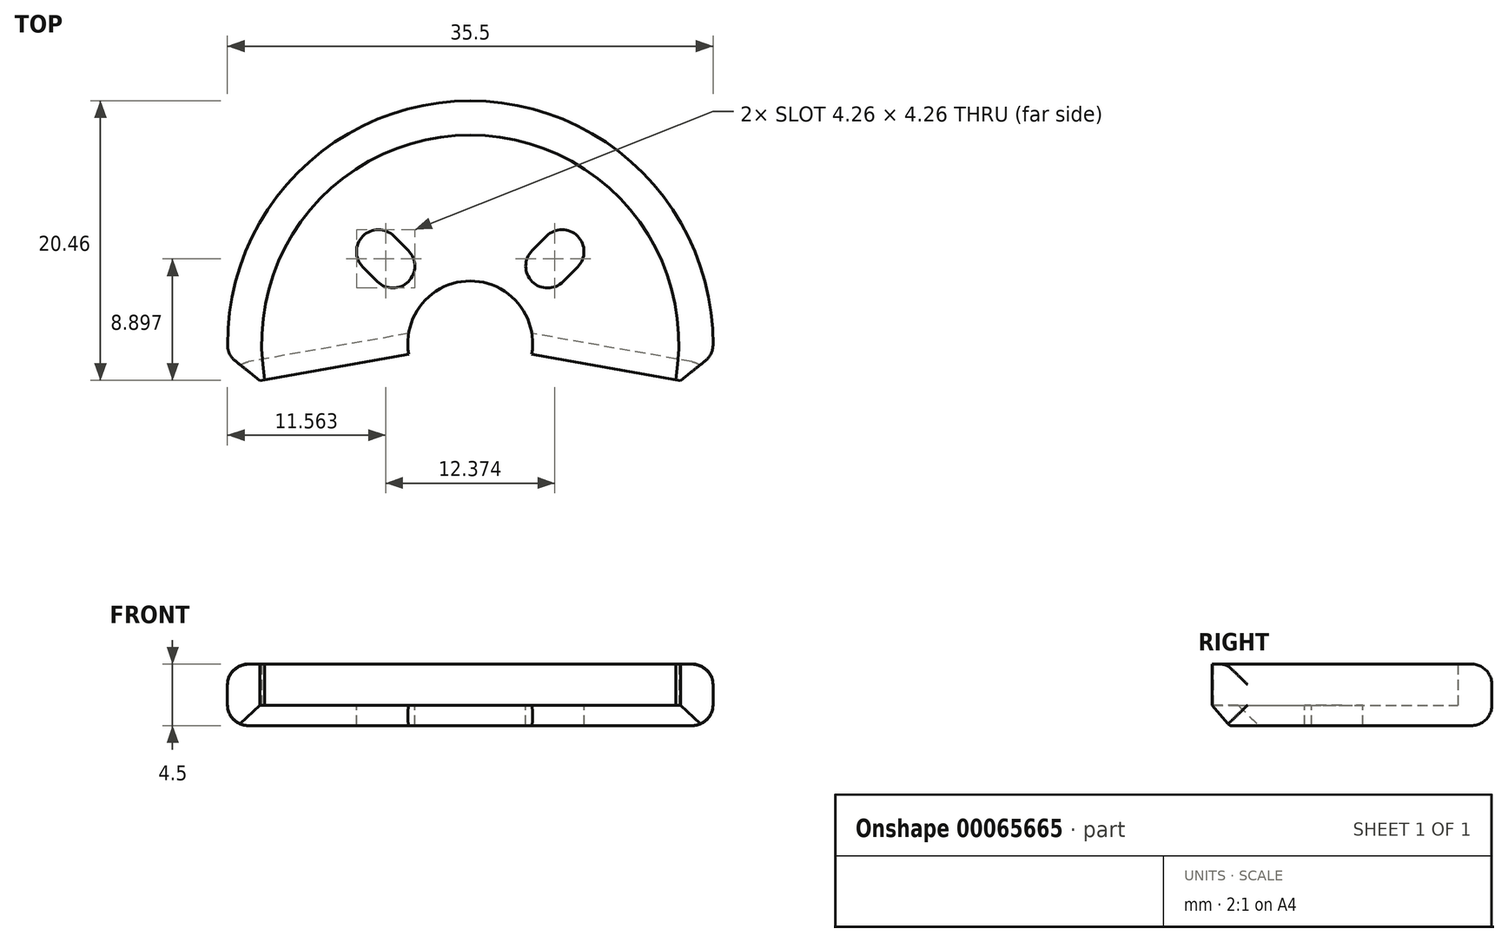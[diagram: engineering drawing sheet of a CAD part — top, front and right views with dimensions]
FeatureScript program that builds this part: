
annotation { "Feature Type Name" : "Feature", "Feature Type Description" : "" }
export const myFeature = defineFeature(function(context is Context, id is Id, definition is map)
    precondition{}
    {
        {
            var Q0;
            Q0=qCreatedBy(makeId("Top.planeOp"),FACE);
            var sketch = newSketch(context, id + "F0", { "sketchPlane" : qUnion([Q0])});
            skLineSegment(sketch, "E0", {"start": v(-4.5, -0.8) * mm, "end": v(-15.02, -2.65) * mm});
            skLineSegment(sketch, "E1", {"start": v(-15.02, -2.65) * mm, "end": v(-17.48, -3.08) * mm});
            skLineSegment(sketch, "E2", {"start": v(0, 0) * mm, "end": v(-5.66, 5.66) * mm, "construction": true});
            skLineSegment(sketch, "E3", {"start": v(-5.66, 5.66) * mm, "end": v(-6.72, 6.72) * mm, "construction": true});
            skArc(sketch, "E4.0.startCap", {"start": v(-4.53, 6.79) * mm, "mid": v(-4.53, 4.53) * mm, "end": v(-6.79, 4.53) * mm});
            skArc(sketch, "E4.0.endCap", {"start": v(-7.85, 5.59) * mm, "mid": v(-7.85, 7.85) * mm, "end": v(-5.59, 7.85) * mm});
            skLineSegment(sketch, "E4.0.left", {"start": v(-6.79, 4.53) * mm, "end": v(-7.85, 5.59) * mm});
            skLineSegment(sketch, "E4.0.right", {"start": v(-4.53, 6.79) * mm, "end": v(-5.59, 7.85) * mm});
            skLineSegment(sketch, "E5", {"start": v(0, 0) * mm, "end": v(-4.5, -0.8) * mm, "construction": true});
            skLineSegment(sketch, "E6.MirrorCS", {"start": v(4.5, -0.8) * mm, "end": v(15.02, -2.65) * mm});
            skLineSegment(sketch, "E7.MirrorCS", {"start": v(15.02, -2.65) * mm, "end": v(17.48, -3.08) * mm});
            skArc(sketch, "E8.MirrorCS", {"start": v(4.53, 6.79) * mm, "mid": v(4.53, 4.53) * mm, "end": v(6.79, 4.53) * mm});
            skArc(sketch, "E9.MirrorCS", {"start": v(7.85, 5.59) * mm, "mid": v(7.85, 7.85) * mm, "end": v(5.59, 7.85) * mm});
            skLineSegment(sketch, "E10.MirrorCS", {"start": v(4.53, 6.79) * mm, "end": v(5.59, 7.85) * mm});
            skLineSegment(sketch, "E11.MirrorCS", {"start": v(6.79, 4.53) * mm, "end": v(7.85, 5.59) * mm});
            skArc(sketch, "E12", {"start": v(-17.48, -3.08) * mm, "mid": v(0, 17.75) * mm, "end": v(17.48, -3.08) * mm});
            skArc(sketch, "E13", {"start": v(-15.02, -2.65) * mm, "mid": v(0, 15.25) * mm, "end": v(15.02, -2.65) * mm});
            skArc(sketch, "E14", {"start": v(-4.5, -0.8) * mm, "mid": v(0, 4.57) * mm, "end": v(4.5, -0.8) * mm});
            skSolve(sketch);
        }
        {
            var Q0;
            Q0=makeQuery(id+"F0.imprint","IMPRINT",FACE,{"disambiguationData":[TD([[makeQuery(id+"F0.imprint","IMPRINT",EDGE,{"derivedFrom":sQuery(id+"F0.wireOp",EDGE,"E1")}),-1.0]])]});
            extrude(context, id + "F1", {"entities" : qUnion([Q0]), "depth" : 3 * mm});
        }
        {
            var Q0;
            Q0=makeQuery(id+"F0.imprint","IMPRINT",FACE,{"disambiguationData":[TD([[makeQuery(id+"F0.imprint","IMPRINT",EDGE,{"derivedFrom":sQuery(id+"F0.wireOp",EDGE,"E1")}),-1.0]])]});
            var Q1;
            Q1=makeQuery(id+"F0.imprint","IMPRINT",FACE,{"disambiguationData":[TD([[makeQuery(id+"F0.imprint","IMPRINT",EDGE,{"derivedFrom":sQuery(id+"F0.wireOp",EDGE,"E0")}),-1.0]])]});
            extrude(context, id + "F2", {"entities" : qUnion([Q0, Q1]), "operationType" : NewBodyOperationType.ADD, "oppositeDirection" : true, "depth" : 1.5 * mm});
        }
        {
            var Q0;
            {var subQ0=sQuery(id+"F0.wireOp",EDGE,"E12");var subQ1=sQuery(id+"F0.wireOp",EDGE,"E1");Q0=makeQuery(id+"F2.boolean.opBoolean","MERGE",EDGE,{"derivedFrom":[makeQuery(id+"F1.opExtrude","SWEPT_EDGE",EDGE,{"disambiguationData":[OSD([subQ1,subQ0])]}),makeQuery(id+"F2.opExtrude","SWEPT_EDGE",EDGE,{"disambiguationData":[OSD([subQ1,subQ0])]})]});}
            var Q1;
            {var subQ0=sQuery(id+"F0.wireOp",EDGE,"E12");var subQ1=sQuery(id+"F0.wireOp",EDGE,"E7.MirrorCS");Q1=makeQuery(id+"F2.boolean.opBoolean","MERGE",EDGE,{"derivedFrom":[makeQuery(id+"F1.opExtrude","SWEPT_EDGE",EDGE,{"disambiguationData":[OSD([subQ1,subQ0])]}),makeQuery(id+"F2.opExtrude","SWEPT_EDGE",EDGE,{"disambiguationData":[OSD([subQ1,subQ0])]})]});}
            chamfer(context, id + "F3", {"entities" : qUnion([Q0, Q1]), "width" : 2 * mm, "tangentPropagation" : true});
        }
        {
            var Q0;
            Q0=makeQuery(id+"F2.opExtrude","CAP_EDGE",EDGE,{"disambiguationData":[OSD([sQuery(id+"F0.wireOp",EDGE,"E6.MirrorCS"),sQuery(id+"F0.wireOp",EDGE,"E7.MirrorCS")])],"isStart":false});
            var Q1;
            Q1=makeQuery(id+"F2.opExtrude","CAP_EDGE",EDGE,{"disambiguationData":[OSD([sQuery(id+"F0.wireOp",EDGE,"E0"),sQuery(id+"F0.wireOp",EDGE,"E1")])],"isStart":false});
            chamfer(context, id + "F4", {"entities" : qUnion([Q0, Q1]), "width" : 1.5 * mm, "tangentPropagation" : true});
        }
        {
            var Q0;
            Q0=makeQuery(id+"F1.opExtrude","CAP_EDGE",EDGE,{"disambiguationData":[OSD([sQuery(id+"F0.wireOp",EDGE,"E12")])],"isStart":false});
            var Q1;
            Q1=makeQuery(id+"F2.opExtrude","CAP_EDGE",EDGE,{"disambiguationData":[OSD([sQuery(id+"F0.wireOp",EDGE,"E12")])],"isStart":false});
            var Q2;
            {var subQ0=sQuery(id+"F0.wireOp",EDGE,"E12");var subQ1=sQuery(id+"F0.wireOp",EDGE,"E1");Q2=makeQuery(id+"F3.opChamfer","BLEND_EDGE",EDGE,{"blendedFrom":[makeQuery(id+"F2.boolean.opBoolean","MERGE",EDGE,{"derivedFrom":[makeQuery(id+"F1.opExtrude","SWEPT_EDGE",EDGE,{"disambiguationData":[OSD([subQ1,subQ0])]}),makeQuery(id+"F2.opExtrude","SWEPT_EDGE",EDGE,{"disambiguationData":[OSD([subQ1,subQ0])]})]}),makeQuery(id+"F2.boolean.opBoolean","MERGE",FACE,{"derivedFrom":[makeQuery(id+"F1.opExtrude","SWEPT_FACE",FACE,{"disambiguationData":[OSD([subQ0])]}),makeQuery(id+"F2.opExtrude","SWEPT_FACE",FACE,{"disambiguationData":[OSD([subQ0])]})]})],"blendedInto":[makeQuery(id+"F2.boolean.opBoolean","MERGE",FACE,{"derivedFrom":[makeQuery(id+"F1.opExtrude","SWEPT_FACE",FACE,{"disambiguationData":[OSD([subQ0])]}),makeQuery(id+"F2.opExtrude","SWEPT_FACE",FACE,{"disambiguationData":[OSD([subQ0])]})]})]});}
            var Q3;
            {var subQ0=sQuery(id+"F0.wireOp",EDGE,"E12");var subQ1=sQuery(id+"F0.wireOp",EDGE,"E7.MirrorCS");Q3=makeQuery(id+"F3.opChamfer","BLEND_EDGE",EDGE,{"blendedFrom":[makeQuery(id+"F2.boolean.opBoolean","MERGE",EDGE,{"derivedFrom":[makeQuery(id+"F1.opExtrude","SWEPT_EDGE",EDGE,{"disambiguationData":[OSD([subQ1,subQ0])]}),makeQuery(id+"F2.opExtrude","SWEPT_EDGE",EDGE,{"disambiguationData":[OSD([subQ1,subQ0])]})]}),makeQuery(id+"F2.boolean.opBoolean","MERGE",FACE,{"derivedFrom":[makeQuery(id+"F1.opExtrude","SWEPT_FACE",FACE,{"disambiguationData":[OSD([subQ0])]}),makeQuery(id+"F2.opExtrude","SWEPT_FACE",FACE,{"disambiguationData":[OSD([subQ0])]})]})],"blendedInto":[makeQuery(id+"F2.boolean.opBoolean","MERGE",FACE,{"derivedFrom":[makeQuery(id+"F1.opExtrude","SWEPT_FACE",FACE,{"disambiguationData":[OSD([subQ0])]}),makeQuery(id+"F2.opExtrude","SWEPT_FACE",FACE,{"disambiguationData":[OSD([subQ0])]})]})]});}
            fillet(context, id + "F5", {"entities" : qUnion([Q0, Q1, Q2, Q3]), "radius" : 1.5 * mm, "tangentPropagation" : true, "allowEdgeOverflow" : false});
        }
    });
